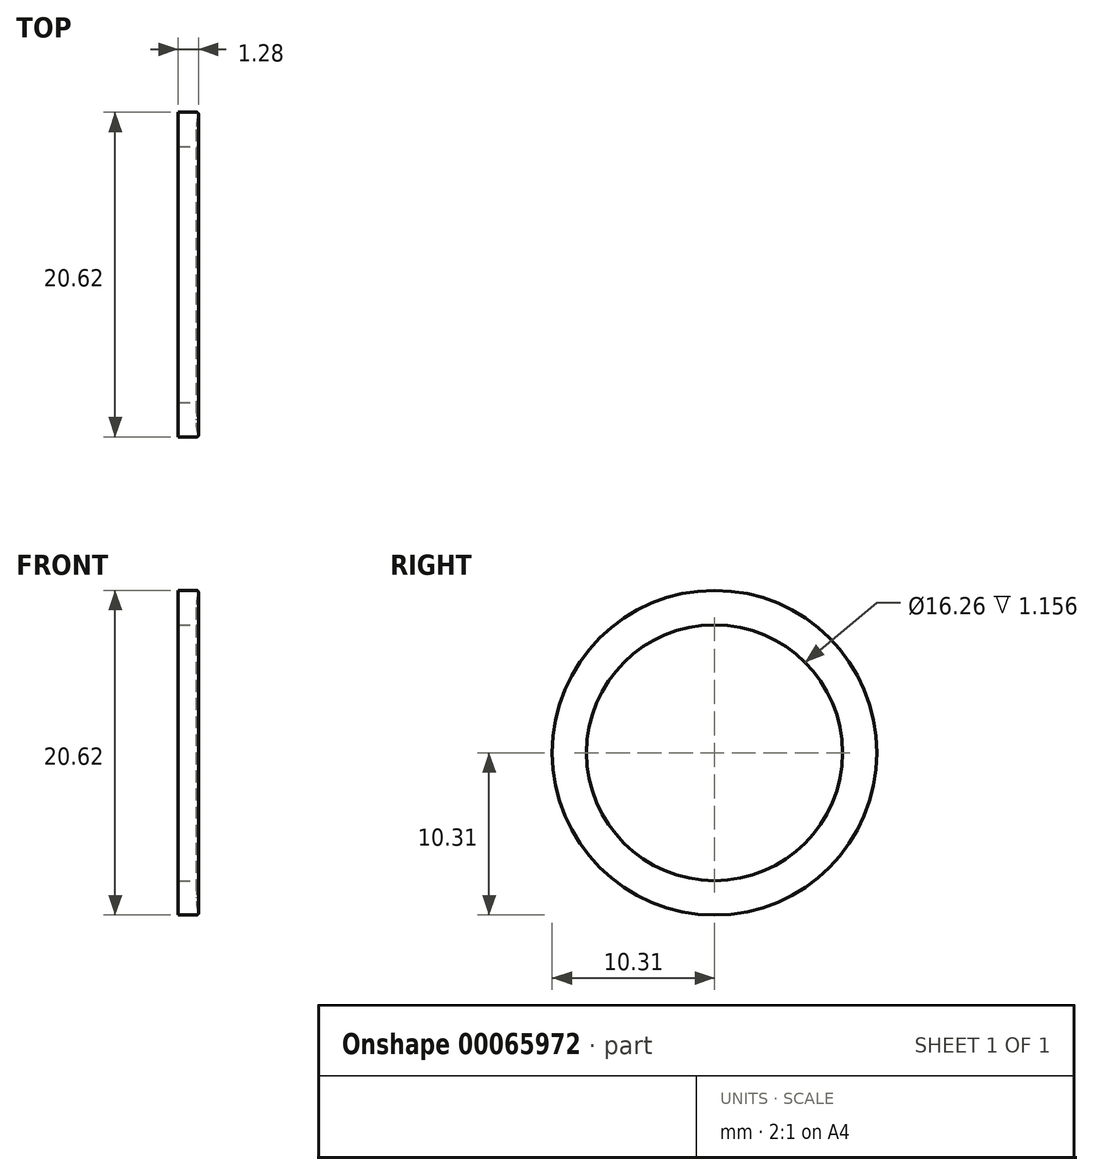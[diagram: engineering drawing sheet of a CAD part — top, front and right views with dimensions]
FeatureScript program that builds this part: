
annotation { "Feature Type Name" : "Feature", "Feature Type Description" : "" }
export const myFeature = defineFeature(function(context is Context, id is Id, definition is map)
    precondition{}
    {
        {
            var Q0;
            Q0=qCreatedBy(makeId("Front.planeOp"),FACE);
            var sketch = newSketch(context, id + "F0", { "sketchPlane" : qUnion([Q0])});
            skLineSegment(sketch, "E0.bottom", {"start": v(-0.17, 10.31) * mm, "end": v(-1.33, 10.31) * mm});
            skLineSegment(sketch, "E0.top", {"start": v(-0.17, 8.13) * mm, "end": v(-1.33, 8.13) * mm});
            skLineSegment(sketch, "E0.right", {"start": v(-1.33, 10.31) * mm, "end": v(-1.33, 8.13) * mm});
            skLineSegment(sketch, "E1", {"start": v(0, 0) * mm, "end": v(-6.16, 0) * mm, "construction": true});
            skArc(sketch, "E2", {"start": v(-0.05, 10.15) * mm, "mid": v(-0.19, 9.22) * mm, "end": v(-0.05, 8.3) * mm});
            skPoint(sketch, "E3.visualSharp", {"position": v(0, 10.31) * mm});
            skArc(sketch, "E3.filletArc", {"start": v(-0.05, 10.15) * mm, "mid": v(-0.07, 10.26) * mm, "end": v(-0.17, 10.31) * mm});
            skPoint(sketch, "E4.visualSharp", {"position": v(0, 8.13) * mm});
            skArc(sketch, "E4.filletArc", {"start": v(-0.17, 8.13) * mm, "mid": v(-0.07, 8.18) * mm, "end": v(-0.05, 8.3) * mm});
            skLineSegment(sketch, "E5", {"start": v(0, 8.13) * mm, "end": v(0, 0) * mm, "construction": true});
            skSolve(sketch);
        }
        {
            var Q0;
            Q0=makeQuery(id+"F0.imprint","IMPRINT",FACE,{"disambiguationData":[TD([[makeQuery(id+"F0.imprint","IMPRINT",EDGE,{"derivedFrom":sQuery(id+"F0.wireOp",EDGE,"E0.bottom")}),1.0]])]});
            var Q1;
            Q1=sQuery(id+"F0.wireOp",EDGE,"E1");
            revolve(context, id + "F1", {"entities" : qUnion([Q0]), "axis" : qUnion([Q1]), "revolveType" : RevolveType.FULL});
        }
    });
